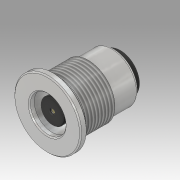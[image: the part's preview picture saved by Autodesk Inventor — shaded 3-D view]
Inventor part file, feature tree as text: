
AUTODESK INVENTOR PART (.ipt)
format: ipt  version: 2019.3 (Build 233278000, 278)  size: 376,832 bytes
history: native  units: mm
features: extrude x16, sketch x16, fillet x4, projected_geometry x2, thread x1, chamfer x1
ambient origin geometry x8: Origin, YZ Plane, XZ Plane, XY Plane, X Axis, Y Axis, Z Axis, Center Point
bodies: Solid1 (feature_tree)
feature tree (40):
  extrude  "Extrusion1"  Depth=1.5mm TaperAngle=0.0deg
  extrude  "Extrusion2"  Depth=1.1mm TaperAngle=0.0deg
  extrude  "Extrusion3"  Depth=6.6mm TaperAngle=0.0deg
  extrude  "Extrusion4"  Depth=5.8mm TaperAngle=0.0deg
  extrude  "Extrusion5"  Depth=1.5mm TaperAngle=0.0deg
  extrude  "Extrusion6"  Depth=9.2mm TaperAngle=0.0deg
  extrude  "Extrusion7"  Depth=8.1mm TaperAngle=0.0deg
  extrude  "Extrusion8"  Depth=4.0mm TaperAngle=0.0deg
  extrude  "Extrusion9"  Depth=12.1mm TaperAngle=0.0deg
  extrude  "Extrusion10"  Depth=12.1mm TaperAngle=0.0deg
  extrude  "Extrusion12"  Depth=1.1mm
  extrude  "Extrusion13"  Depth=1.8mm
  extrude  "Extrusion14"  Depth=0.3mm
  extrude  "Extrusion15"  Depth=0.5mm
  thread  "Thread1"  [1 undecoded]
  chamfer  "Chamfer1"  Distance=0.25mm
  fillet  "Fillet1"  Radius=0.25mm
  fillet  "Fillet2"  Radius=0.25mm
  fillet  "Fillet3"  Radius=0.25mm
  extrude  "Extrusion16"  Depth=2.6mm
  extrude  "Extrusion17"  Depth=1.0mm
  fillet  "Fillet4"  Radius=2.0mm
  sketch  "Sketch1"  dims[d0=15.0mm d1=1.5mm d2=0.0mm]
  sketch  "Sketch2"  dims[d3=12.0mm d4=1.1mm d5=0.0mm]
  sketch  "Sketch3"  dims[d6=11.99mm d7=6.6mm d8=0.0mm]
  sketch  "Sketch4"  dims[d9=11.0mm d10=5.8mm d11=0.0mm]
  sketch  "Sketch5"  dims[d12=8.8mm d13=1.5mm d14=0.0mm]
  sketch  "Sketch6"  dims[d15=8.0mm d16=9.2mm d17=0.0mm]
  sketch  "Sketch7"  dims[d18=9.0mm d19=8.1mm d20=0.0mm]
  sketch  "Sketch8"  dims[d21=7.0mm d22=4.0mm d23=0.0mm]
  sketch  "Sketch9"  dims[d24=5.4mm d25=12.1mm d26=0.0mm]
  sketch  "Sketch10"  dims[d27=1.0mm d28=12.1mm d29=0.0mm]
  sketch  "Sketch12"  dims[d33=0.3mm d38=1.1mm]
  sketch  "Sketch13"  dims[d39=0.3mm d40=1.8mm]
  sketch  "Sketch14"  dims[d48=0.3mm d49=1.600003mm]
  sketch  "Sketch15"  dims[d50=1.600003mm d51=0.5mm d52=4.5mm]
  sketch  "Sketch16"  dims[d53=2.0mm]
  projected_geometry  "Projected Loop4"
  sketch  "Sketch17"  dims[d54=1.2mm d55=1.2mm d56=0.0mm d57=0.0mm d58=0.25mm d59=0.25mm d60=0.25mm d61=0.25mm d62=2.6mm d63=1.0mm d64=2.0mm d65=0.5mm d66=0.0mm d67=1.1mm d68=1.1mm d69=0.0mm d70=0.0mm d71=1.54mm d72=1.2mm d73=1.2mm d74=0.0mm d75=0.0mm d76=0.25mm d77=0.25mm d78=0.25mm d79=0.25mm d80=1.05mm d81=2.2mm d82=0.25mm d83=2.1mm d84=1.1mm d85=1.1mm d86=0.0mm d87=0.0mm d88=10.0mm d89=0.0mm d90=0.25mm d91=2.0mm d92=45.0deg d93=0.25mm d94=0.5mm d95=0.25mm d99=2.2mm d100=2.2mm d101=0.25mm d102=0.35mm d103=0.75mm d104=2.7mm d105=0.0mm d106=1.5mm d107=1.0mm d108=2.7mm d109=0.0mm d110=0.5mm]
  projected_geometry  "Projected Loop5"
note: 1 required parameter value undecoded (feature->parameter linkage not recoverable at this tier; creation-order binding heuristic only, values carry confidence <= 0.55)
